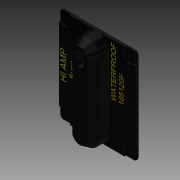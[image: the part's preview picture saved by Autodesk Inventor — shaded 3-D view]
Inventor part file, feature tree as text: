
AUTODESK INVENTOR PART (.ipt)
format: ipt  version: 2018 (Build 220112000, 112)  size: 824,320 bytes
history: native  units: mm (DEFAULTED — no unit token found)
features: sketch x6, extrude x4, plane x2, mirror x2, emboss x2, chamfer x1, reference x1
ambient origin geometry x8: Origin, YZ Plane, XZ Plane, XY Plane, X Axis, Y Axis, Z Axis, Center Point
bodies: Solid1 (feature_tree)
feature tree (18):
  extrude  "Extrusion1"  Depth=6.35mm
  extrude  "Extrusion2"  Depth=2.54mm
  chamfer  "Chamfer2"  Distance=8.89mm
  extrude  "Extrusion3"  Depth=0.762mm
  plane  "Work Plane1"
  plane  "Work Plane2"
  extrude  "Extrusion5"  Depth=0.0508mm TaperAngle=0.0deg
  mirror  "Mirror3"
  mirror  "Mirror4"
  emboss  "Emboss1"
  emboss  "Emboss2"
  sketch  "Sketch1"  dims[d0=1.524mm d1=0.0mm d2=6.35mm]
  reference  "Reference1"
  sketch  "Sketch2"  dims[d3=8.89mm d4=0.0mm d7=3.81mm d8=2.54mm]
  sketch  "Sketch3"  dims[d10=2.159mm]
  sketch  "Sketch5"  dims[d11=7.62mm d12=8.89mm d13=0.0mm]
  sketch  "Sketch6"  dims[d17=6.35mm d18=0.762mm]
  sketch  "Sketch7"  dims[d19=0.762mm d20=0.762mm d21=0.0mm d22=0.0508mm d23=0.0mm d24=0.0508mm d25=0.0mm d26=45.0deg]
